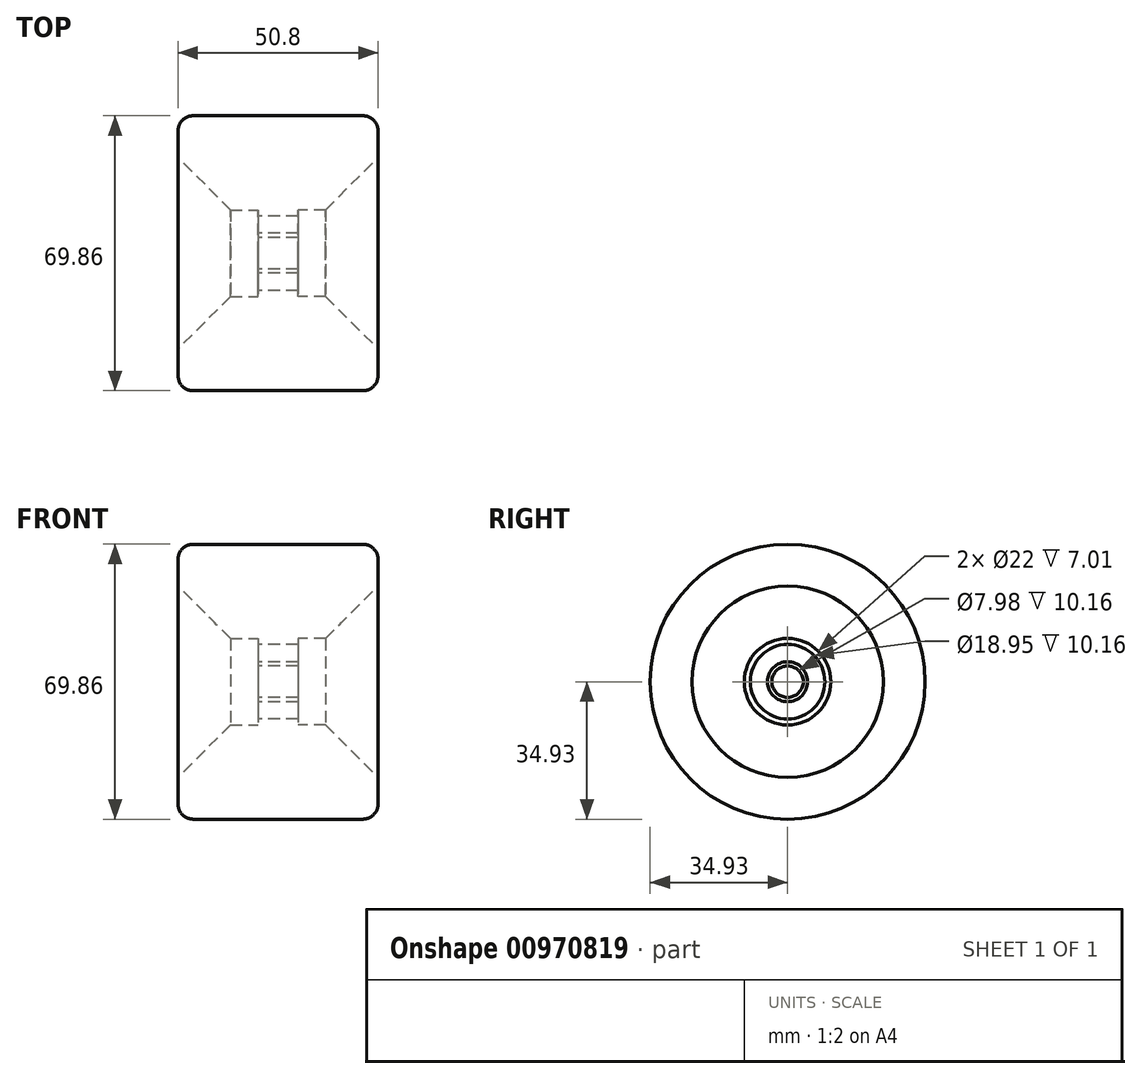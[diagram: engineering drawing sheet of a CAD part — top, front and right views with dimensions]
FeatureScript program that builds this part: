
annotation { "Feature Type Name" : "Feature", "Feature Type Description" : "" }
export const myFeature = defineFeature(function(context is Context, id is Id, definition is map)
    precondition{}
    {
        {
            var Q0;
            Q0=qCreatedBy(makeId("Front.planeOp"),FACE);
            var sketch = newSketch(context, id + "F0", { "sketchPlane" : qUnion([Q0])});
            skLineSegment(sketch, "E0.left", {"start": v(0, 34.92) * mm, "end": v(0, 9.47) * mm});
            skPoint(sketch, "E1", {"position": v(0, 9.47) * mm});
            skPoint(sketch, "E0.top.start.orphan", {"position": v(0, 0) * mm});
            skLineSegment(sketch, "E2", {"start": v(0, 9.47) * mm, "end": v(5.08, 9.47) * mm});
            skLineSegment(sketch, "E3", {"start": v(5.08, 9.47) * mm, "end": v(5.08, 11) * mm});
            skLineSegment(sketch, "E4", {"start": v(5.08, 11) * mm, "end": v(12.1, 11) * mm});
            skLineSegment(sketch, "E5", {"start": v(12.1, 11) * mm, "end": v(25.4, 24.3) * mm});
            skLineSegment(sketch, "E6", {"start": v(12.1, 11) * mm, "end": v(29.68, 11) * mm, "construction": true});
            skLineSegment(sketch, "E7", {"start": v(0, 0) * mm, "end": v(17.2, 0) * mm, "construction": true});
            skLineSegment(sketch, "E8", {"start": v(0, 34.92) * mm, "end": v(21.59, 34.93) * mm});
            skLineSegment(sketch, "E9", {"start": v(25.4, 31.12) * mm, "end": v(25.4, 24.3) * mm});
            skArc(sketch, "E10.filletArc", {"start": v(25.4, 31.12) * mm, "mid": v(24.28, 33.8) * mm, "end": v(21.59, 34.93) * mm});
            skSolve(sketch);
        }
        {
            var Q0;
            Q0 = qSketchRegion(id + "F0", true);
            var Q1;
            Q1=sQuery(id+"F0.wireOp",EDGE,"E7");
            revolve(context, id + "F1", {"surfaceOperationType" : NewSurfaceOperationType.NEW, "entities" : qUnion([Q0]), "axis" : qUnion([Q1]), "revolveType" : RevolveType.FULL});
        }
        {
            var Q0;
            Q0=makeQuery(id+"F1.opRevolve","SWEPT_BODY",BODY,{"disambiguationData":[OSD([sQuery(id+"F0.wireOp",EDGE,"E0.left"),sQuery(id+"F0.wireOp",EDGE,"E2"),sQuery(id+"F0.wireOp",EDGE,"E3"),sQuery(id+"F0.wireOp",EDGE,"E4"),sQuery(id+"F0.wireOp",EDGE,"E5"),sQuery(id+"F0.wireOp",EDGE,"E8"),sQuery(id+"F0.wireOp",EDGE,"E9"),sQuery(id+"F0.wireOp",EDGE,"E10.filletArc")])]});
            var Q1;
            Q1=qCreatedBy(makeId("Right.planeOp"),FACE);
            mirror(context, id + "F2", {"operationType" : NewBodyOperationType.ADD, "entities" : qUnion([Q0]), "mirrorPlane" : qUnion([Q1])});
        }
        {
            var Q0;
            Q0=qCreatedBy(makeId("Front.planeOp"),FACE);
            var sketch = newSketch(context, id + "F3", { "sketchPlane" : qUnion([Q0])});
            skLineSegment(sketch, "E11.bottom", {"start": v(-5.08, 5.08) * mm, "end": v(5.08, 5.08) * mm});
            skLineSegment(sketch, "E11.top", {"start": v(-5.08, 3.99) * mm, "end": v(5.08, 3.99) * mm});
            skLineSegment(sketch, "E11.left", {"start": v(-5.08, 5.08) * mm, "end": v(-5.08, 3.99) * mm});
            skLineSegment(sketch, "E11.right", {"start": v(5.08, 5.08) * mm, "end": v(5.08, 3.99) * mm});
            skSolve(sketch);
        }
        {
            var Q0;
            Q0 = qSketchRegion(id + "F3", true);
            var Q1;
            Q1=sQuery(id+"F0.wireOp",EDGE,"E7");
            revolve(context, id + "F4", {"surfaceOperationType" : NewSurfaceOperationType.NEW, "entities" : qUnion([Q0]), "axis" : qUnion([Q1]), "revolveType" : RevolveType.FULL});
        }
    });
